# Revit family: ADB Electric grills cupboard 610
name_source: partatom
category: Equipement spécialisé
units: mm (PartAtom-declared; Revit-internal decimal feet)

## family parameters
Basée sur le plan de construction = Non
Conserver l'orientation des annotations = Non
Cote de connecteur circulaire = Utiliser le diamètre
Couper avec des vides une fois chargée = Non
Numéro OmniClass = 23.40.40.14.17.11
Partagée = Non
Repère de localisation dans la pièce = Non
Titre OmniClass = Cookers, Ovens, Stoves
Toujours verticalement = Oui
Type d'élément = Normal

## types (6) — shared parameters
C = 300 mm  [stored 0.984252 ft]
Commentaires du type = Ambassade range - Electric grills & plancha
D = 740 mm  [stored 2.42782 ft]
Fabricant = Société Industrielle de Lacanche
URL = https://www.ambassade-de-bourgogne.com
URL Cutsheet = https://www.ambassade-de-bourgogne.com
zero-valued in all types: Elévation par défaut

## per-type parameters (varying)
| type | Description | Table |
| CME 610 SRKC | Ridged chrome electric grill cupboard | CME_CMG 610 SLK_SLKC_SRK_SRKC_SLR_SLRC : SRKC |
| CME 610 SRK | Ridged steel electric grill cupboard | CME_CMG 610 SLK_SLKC_SRK_SRKC_SLR_SLRC : SRK |
| CME 610 SLK | Smooth steel electric grill cupboard | CME_CMG 610 SLK_SLKC_SRK_SRKC_SLR_SLRC : SLK |
| CME 610 SLKC | Smooth chrome electric grill cupboard | CME_CMG 610 SLK_SLKC_SRK_SRKC_SLR_SLRC : SLKC |
| CME 610 SLR | Half-ridged, half smooth steel electric grill cupboard | CME_CMG 610 SLK_SLKC_SRK_SRKC_SLR_SLRC : SLR |
| CME 610 SLRC | Half-ridged, half smooth chrome electric grill cupboard | CME_CMG 610 SLK_SLKC_SRK_SRKC_SLR_SLRC : SLRC |

note: column(s) folded — value = type name in every type: Modèle

note: [stored X ft] marks values corroborated as IEEE doubles in the binary element streams (Revit-internal decimal feet)
